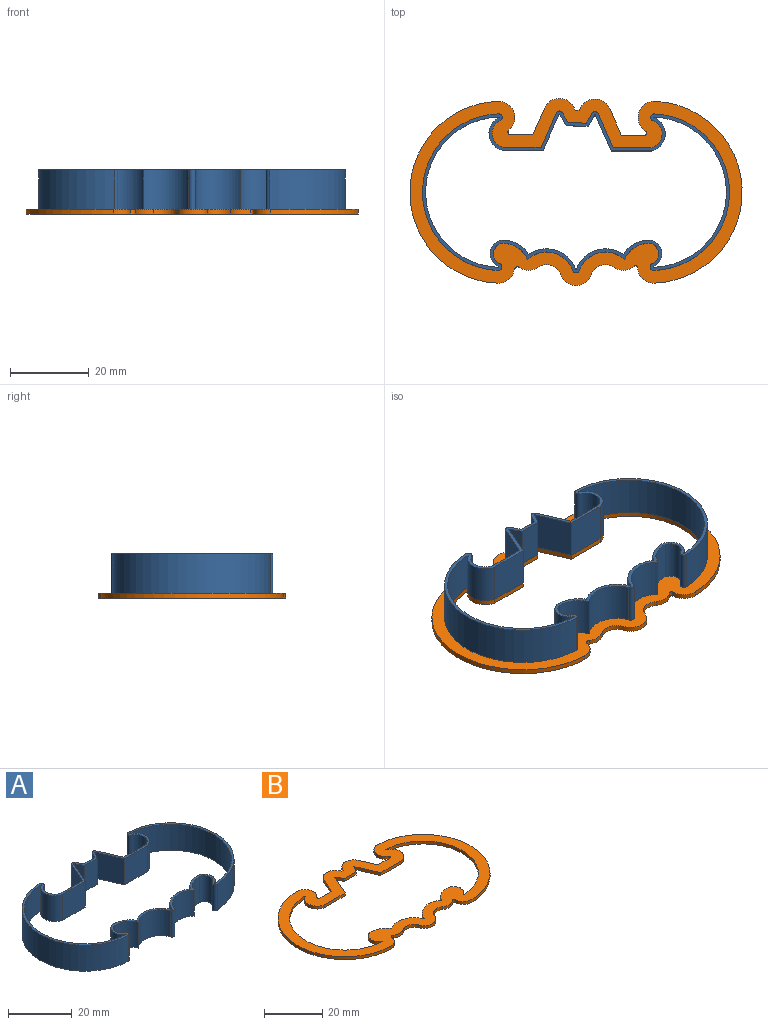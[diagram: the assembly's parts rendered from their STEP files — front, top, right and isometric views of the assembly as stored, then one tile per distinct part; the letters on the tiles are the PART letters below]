
ASSEMBLY  parts=2 mates=1
PART A: 50 faces, bbox 77.8x41x10 mm
  f0: cylinder r=3.58mm len=10mm, axis (0,0,-1), area 92.1mm2, adj f1,f47,f48,f49
  f1: plane 10x9.56mm, normal (0,1,0), area 95.6mm2, adj f0,f2,f48,f49
  f2: plane 10x8.64mm, normal (0.92,0.4,0), area 94.3mm2, adj f1,f3,f48,f49
  f3: cylinder r=0.9mm len=10mm, axis (0,0,-1), area 19.9mm2, adj f2,f4,f48,f49
  f4: plane 10x2.48mm, normal (-0.87,0.5,0), area 28.5mm2, adj f3,f5,f48,f49
  f5: plane 10x4.62mm, normal (0.03,1,0), area 46.3mm2, adj f4,f6,f48,f49
  f6: plane 10x2.5mm, normal (0.87,0.5,0), area 28.8mm2, adj f5,f7,f48,f49
  f7: cylinder r=0.9mm len=10mm, axis (0,0,-1), area 19.9mm2, adj f6,f8,f48,f49
  f8: plane 10x8.64mm, normal (-0.92,0.4,0), area 94.3mm2, adj f7,f9,f48,f49
  f9: plane 10x9.56mm, normal (0,1,0), area 95.6mm2, adj f8,f10,f48,f49
  f10: cylinder r=3.58mm len=10mm, axis (0,0,-1), area 89.3mm2, adj f9,f11,f48,f49
  f11: cylinder r=0.9mm len=10mm, axis (0,0,-1), area 24.6mm2, adj f10,f12,f48,f49
  f12: cylinder r=19.85mm len=39.68mm, axis (0,0,-1), area 611.2mm2, adj f11,f13,f48,f49
  f13: cylinder r=0.9mm len=10mm, axis (0,0,-1), area 24.9mm2, adj f12,f14,f48,f49
  f14: cylinder r=2.72mm len=10mm, axis (0,0,-1), area 67.3mm2, adj f13,f15,f48,f49
  f15: cylinder r=6.61mm len=10mm, axis (0,0,-1), area 83.1mm2, adj f14,f16,f48,f49
  f16: cylinder r=7.03mm len=11.45mm, axis (0,0,-1), area 139.7mm2, adj f15,f17,f48,f49
  f17: cylinder r=0.9mm len=10mm, axis (0,0,-1), area 22.2mm2, adj f16,f18,f48,f49
  f18: cylinder r=7.03mm len=11.45mm, axis (0,0,-1), area 139.7mm2, adj f17,f19,f48,f49
  f19: cylinder r=6.61mm len=10mm, axis (0,0,-1), area 83.1mm2, adj f18,f20,f48,f49
  f20: cylinder r=2.72mm len=10mm, axis (0,0,-1), area 67.3mm2, adj f19,f21,f48,f49
  f21: cylinder r=0.9mm len=10mm, axis (0,0,-1), area 24.9mm2, adj f20,f22,f48,f49
  f22: cylinder r=19.85mm len=39.67mm, axis (0,0,-1), area 608.6mm2, adj f21,f47,f48,f49
  f23: cylinder r=4.38mm len=10mm, axis (0,0,-1), area 113.6mm2, adj f24,f46,f48,f49
  f24: cylinder r=0.1mm len=10mm, axis (0,0,-1), area 2.8mm2, adj f23,f25,f48,f49
  f25: cylinder r=19.05mm len=38.07mm, axis (0,0,-1), area 584.1mm2, adj f24,f26,f48,f49
  f26: cylinder r=0.1mm len=10mm, axis (0,0,-1), area 2.8mm2, adj f25,f27,f48,f49
  f27: cylinder r=3.52mm len=10mm, axis (0,0,-1), area 87.8mm2, adj f26,f28,f48,f49
  f28: cylinder r=7.41mm len=10mm, axis (0,0,-1), area 83.2mm2, adj f27,f29,f48,f49
  f29: cylinder r=7.83mm len=11.94mm, axis (0,0,-1), area 145mm2, adj f28,f30,f48,f49
  f30: cylinder r=0.1mm len=10mm, axis (0,0,-1), area 2.5mm2, adj f29,f31,f48,f49
  f31: cylinder r=7.83mm len=11.94mm, axis (0,0,-1), area 145mm2, adj f30,f32,f48,f49
  f32: cylinder r=7.41mm len=10mm, axis (0,0,-1), area 83.2mm2, adj f31,f33,f48,f49
  f33: cylinder r=3.52mm len=10mm, axis (0,0,-1), area 87.8mm2, adj f32,f34,f48,f49
  f34: cylinder r=0.1mm len=10mm, axis (0,0,-1), area 2.8mm2, adj f33,f35,f48,f49
  f35: cylinder r=19.05mm len=38.08mm, axis (0,0,-1), area 586.6mm2, adj f34,f36,f48,f49
  f36: cylinder r=0.1mm len=10mm, axis (0,0,-1), area 2.7mm2, adj f35,f37,f48,f49
  f37: cylinder r=4.38mm len=10mm, axis (0,0,-1), area 110.1mm2, adj f36,f38,f48,f49
  f38: plane 10.16x10mm, normal (0,-1,0), area 101.6mm2, adj f37,f39,f48,f49
  f39: plane 10x9.12mm, normal (0.92,-0.4,0), area 99.5mm2, adj f38,f40,f48,f49
  f40: cylinder r=0.1mm len=10mm, axis (0,0,-1), area 2.2mm2, adj f39,f41,f48,f49
  f41: plane 10x2.89mm, normal (-0.87,-0.5,0), area 33.3mm2, adj f40,f42,f48,f49
  f42: plane 10x5.55mm, normal (-0.03,-1,0), area 55.5mm2, adj f41,f43,f48,f49
  f43: plane 10x2.89mm, normal (0.87,-0.5,0), area 33.3mm2, adj f42,f44,f48,f49
  f44: cylinder r=0.1mm len=10mm, axis (0,0,-1), area 2.2mm2, adj f43,f45,f48,f49
  f45: plane 10x9.12mm, normal (-0.92,-0.4,0), area 99.5mm2, adj f44,f46,f48,f49
  f46: plane 10.16x10mm, normal (0,-1,0), area 101.6mm2, adj f23,f45,f48,f49
  f47: cylinder r=0.9mm len=10mm, axis (0,0,-1), area 25.4mm2, adj f0,f22,f48,f49
  f48: plane 77.8x41.01mm, normal (0,0,1), area 207.8mm2, adj f0,f1,f2,f3,f4,f5,f6,f7
  f49: plane 77.8x41.01mm, normal (0,0,-1), area 207.8mm2, adj f0,f1,f2,f3,f4,f5,f6,f7
PART B: 52 faces, bbox 84.2x47.4x1.2 mm
  f0: cylinder r=19.05mm len=38.07mm, axis (0,0,-1), area 70.1mm2, adj f1,f49,f50,f51
  f1: cylinder r=0.1mm len=1.2mm, axis (0,0,-1), area 0.3mm2, adj f0,f2,f50,f51
  f2: cylinder r=3.52mm len=6.65mm, axis (0,0,-1), area 10.5mm2, adj f1,f3,f50,f51
  f3: cylinder r=7.41mm len=6.96mm, axis (0,0,-1), area 9.9mm2, adj f2,f4,f50,f51
  f4: cylinder r=0.1mm len=1.2mm, axis (0,0,-1), area 0.2mm2, adj f3,f5,f50,f51
  f5: cylinder r=7.83mm len=11.85mm, axis (0,0,-1), area 17.3mm2, adj f4,f6,f50,f51
  f6: cylinder r=0.1mm len=1.2mm, axis (0,0,-1), area 0.3mm2, adj f5,f7,f50,f51
  f7: cylinder r=7.83mm len=11.85mm, axis (0,0,-1), area 17.3mm2, adj f6,f8,f50,f51
  f8: cylinder r=0.1mm len=1.2mm, axis (0,0,-1), area 0.2mm2, adj f7,f9,f50,f51
  f9: cylinder r=7.41mm len=6.96mm, axis (0,0,-1), area 9.9mm2, adj f8,f10,f50,f51
  f10: cylinder r=3.52mm len=6.65mm, axis (0,0,-1), area 10.5mm2, adj f9,f11,f50,f51
  f11: cylinder r=0.1mm len=1.2mm, axis (0,0,-1), area 0.3mm2, adj f10,f12,f50,f51
  f12: cylinder r=19.05mm len=38.08mm, axis (0,0,-1), area 70.4mm2, adj f11,f13,f50,f51
  f13: cylinder r=0.1mm len=1.2mm, axis (0,0,-1), area 0.3mm2, adj f12,f14,f50,f51
  f14: cylinder r=4.38mm len=8.26mm, axis (0,0,-1), area 13.2mm2, adj f13,f15,f50,f51
  f15: plane 10.16x1.2mm, normal (0,-1,0), area 12.2mm2, adj f14,f16,f50,f51
  f16: plane 9.12x4mm, normal (0.92,-0.4,0), area 11.9mm2, adj f15,f17,f50,f51
  f17: cylinder r=0.1mm len=1.2mm, axis (0,0,-1), area 0.3mm2, adj f16,f18,f50,f51
  f18: plane 2.89x1.65mm, normal (-0.87,-0.5,0), area 4mm2, adj f17,f19,f50,f51
  f19: plane 5.55x1.2mm, normal (-0.03,-1,0), area 6.7mm2, adj f18,f20,f50,f51
  f20: plane 2.89x1.65mm, normal (0.87,-0.5,0), area 4mm2, adj f19,f21,f50,f51
  f21: cylinder r=0.1mm len=1.2mm, axis (0,0,-1), area 0.3mm2, adj f20,f22,f50,f51
  f22: plane 9.12x4mm, normal (-0.92,-0.4,0), area 11.9mm2, adj f21,f23,f50,f51
  f23: plane 10.16x1.2mm, normal (0,-1,0), area 12.2mm2, adj f22,f24,f50,f51
  f24: cylinder r=4.38mm len=8.39mm, axis (0,0,-1), area 13.6mm2, adj f23,f49,f50,f51
  f25: cylinder r=4.1mm len=4.24mm, axis (0,0,-1), area 7.7mm2, adj f26,f48,f50,f51
  f26: cylinder r=23.05mm len=46.07mm, axis (0,0,-1), area 84.8mm2, adj f25,f27,f50,f51
  f27: cylinder r=4.1mm len=7.6mm, axis (0,0,-1), area 13mm2, adj f26,f28,f50,f51
  f28: cylinder r=0.55mm len=1.2mm, axis (0,0,-1), area 1.6mm2, adj f27,f29,f50,f51
  f29: plane 5.88x1.2mm, normal (0,1,0), area 7.1mm2, adj f28,f30,f50,f51
  f30: plane 6.72x2.95mm, normal (0.92,0.4,0), area 8.8mm2, adj f29,f31,f50,f51
  f31: cylinder r=4.1mm len=7.32mm, axis (0,0,-1), area 10.9mm2, adj f30,f32,f50,f51
  f32: plane 1.2x0.81mm, normal (-0.87,0.5,0), area 1.1mm2, adj f31,f33,f50,f51
  f33: plane 1.2x0.91mm, normal (0.03,1,0), area 1.1mm2, adj f32,f34,f50,f51
  f34: plane 1.2x0.94mm, normal (0.87,0.5,0), area 1.3mm2, adj f33,f35,f50,f51
  f35: cylinder r=4.1mm len=7.32mm, axis (0,0,-1), area 10.9mm2, adj f34,f36,f50,f51
  f36: plane 6.72x2.95mm, normal (-0.92,0.4,0), area 8.8mm2, adj f35,f37,f50,f51
  f37: plane 5.71x1.2mm, normal (0,1,0), area 6.9mm2, adj f36,f38,f50,f51
  f38: cylinder r=0.65mm len=1.2mm, axis (0,0,-1), area 1.9mm2, adj f37,f39,f50,f51
  f39: cylinder r=4.1mm len=7.3mm, axis (0,0,-1), area 12.3mm2, adj f38,f40,f50,f51
  f40: cylinder r=23.05mm len=46.08mm, axis (0,0,-1), area 85.2mm2, adj f39,f41,f50,f51
  f41: cylinder r=4.1mm len=4.19mm, axis (0,0,-1), area 7.1mm2, adj f40,f42,f50,f51
  f42: cylinder r=0.89mm len=1.31mm, axis (0,0,-1), area 2mm2, adj f41,f43,f50,f51
  f43: cylinder r=4.1mm len=4.68mm, axis (0,0,-1), area 6mm2, adj f42,f44,f50,f51
  f44: cylinder r=3.83mm len=5.8mm, axis (0,0,-1), area 8.5mm2, adj f43,f45,f50,f51
  f45: cylinder r=4.1mm len=7.73mm, axis (0,0,-1), area 12.1mm2, adj f44,f46,f50,f51
  f46: cylinder r=3.83mm len=5.8mm, axis (0,0,-1), area 8.5mm2, adj f45,f47,f50,f51
  f47: cylinder r=4.1mm len=5.07mm, axis (0,0,-1), area 6.6mm2, adj f46,f48,f50,f51
  f48: cylinder r=0.55mm len=1.2mm, axis (0,0,-1), area 1.3mm2, adj f25,f47,f50,f51
  f49: cylinder r=0.1mm len=1.2mm, axis (0,0,-1), area 0.3mm2, adj f0,f24,f50,f51
  f50: plane 84.2x47.41mm, normal (0,0,1), area 1073.7mm2, adj f0,f1,f2,f3,f4,f5,f6,f7
  f51: plane 84.2x47.41mm, normal (0,0,-1), area 1073.7mm2, adj f0,f1,f2,f3,f4,f5,f6,f7
PLACE A t=(0,0,1.2)mm
PLACE B at identity
MATE fastened A.f49 <-> B.f50  axis (0,0,-1) through (14.48,10.59,1.2)mm
